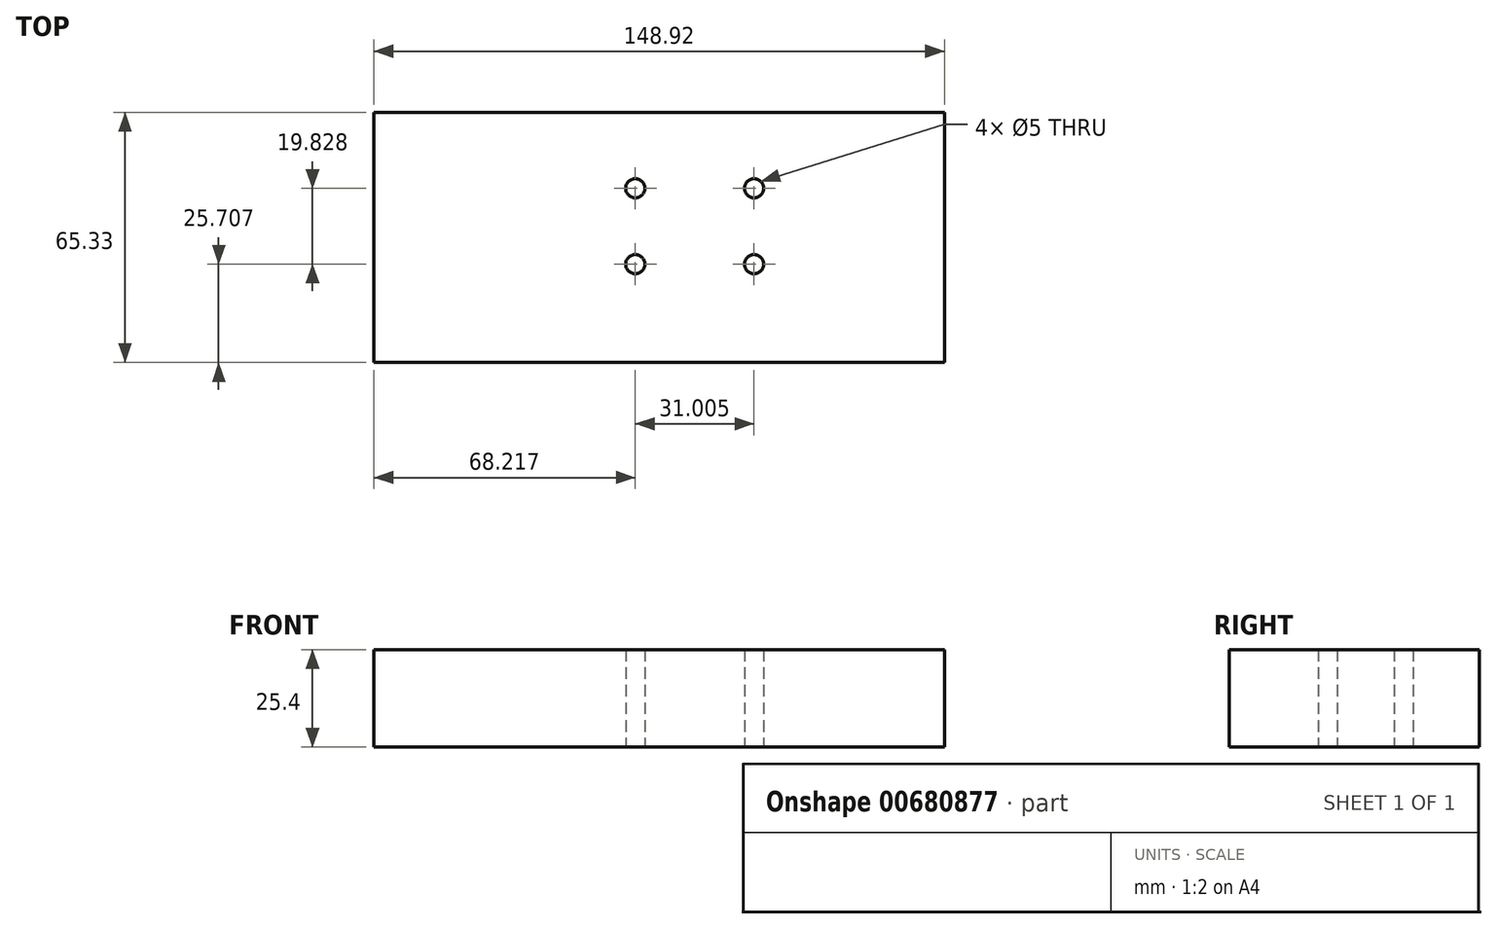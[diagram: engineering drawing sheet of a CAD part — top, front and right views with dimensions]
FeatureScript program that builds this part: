
annotation { "Feature Type Name" : "Feature", "Feature Type Description" : "" }
export const myFeature = defineFeature(function(context is Context, id is Id, definition is map)
    precondition{}
    {
        {
            var Q0;
            Q0=qCreatedBy(makeId("Top.planeOp"),FACE);
            var sketch = newSketch(context, id + "F0", { "sketchPlane" : qUnion([Q0])});
            skLineSegment(sketch, "E0.bottom", {"start": v(-106.28, 12.9) * mm, "end": v(42.64, 12.9) * mm});
            skLineSegment(sketch, "E0.top", {"start": v(-106.28, -52.43) * mm, "end": v(42.64, -52.43) * mm});
            skLineSegment(sketch, "E0.left", {"start": v(-106.28, 12.9) * mm, "end": v(-106.28, -52.43) * mm});
            skLineSegment(sketch, "E0.right", {"start": v(42.64, 12.9) * mm, "end": v(42.64, -52.43) * mm});
            skPoint(sketch, "E1", {"position": v(-63.68, -30.46) * mm});
            skPoint(sketch, "E2", {"position": v(-21.6, -30.46) * mm});
            skPoint(sketch, "E3", {"position": v(-21.6, -9.02) * mm});
            skPoint(sketch, "E4", {"position": v(-63.68, -9.02) * mm});
            skSolve(sketch);
        }
        {
            var Q0;
            Q0 = qSketchRegion(id + "F0", true);
            extrude(context, id + "F1", {"entities" : qUnion([Q0]), "depth" : 25.4 * mm, "offsetDistance" : 25.4 * mm});
        }
        {
            var Q0;
            Q0=makeQuery(id+"F1.opExtrude","CAP_FACE",FACE,{"disambiguationData":[OSD([sQuery(id+"F0.wireOp",EDGE,"E0.bottom"),sQuery(id+"F0.wireOp",EDGE,"E0.top"),sQuery(id+"F0.wireOp",EDGE,"E0.left"),sQuery(id+"F0.wireOp",EDGE,"E0.right")])],"isStart":true});
            var sketch = newSketch(context, id + "F2", { "sketchPlane" : qUnion([Q0])});
            skPoint(sketch, "E5", {"position": v(-7.06, 26.72) * mm});
            skPoint(sketch, "E6", {"position": v(-7.06, 6.9) * mm});
            skPoint(sketch, "E7", {"position": v(-38.06, 6.9) * mm});
            skPoint(sketch, "E8", {"position": v(-38.06, 26.72) * mm});
            skSolve(sketch);
        }
        {
            var Q0;
            Q0=sQuery(id+"F2.wireOp",VERTEX,"E5");
            var Q1;
            Q1=sQuery(id+"F2.wireOp",VERTEX,"E6");
            var Q2;
            Q2=sQuery(id+"F2.wireOp",VERTEX,"E8");
            var Q3;
            Q3=sQuery(id+"F2.wireOp",VERTEX,"E7");
            var Q4;
            Q4=makeQuery(id+"F1.opExtrude","SWEPT_BODY",BODY,{"disambiguationData":[OSD([sQuery(id+"F0.wireOp",EDGE,"E0.bottom"),sQuery(id+"F0.wireOp",EDGE,"E0.top"),sQuery(id+"F0.wireOp",EDGE,"E0.left"),sQuery(id+"F0.wireOp",EDGE,"E0.right")])]});
            hole(context, id + "F3", {"style" : HoleStyle.SIMPLE, "endStyle" : HoleEndStyle.THROUGH, "standardTappedOrClearance" : lookupTablePath({ "standard" : "ISO", "size" : "5", "type" : "Drilled" }), "standardBlindInLast" : lookupTablePath({ "standard" : "ISO", "size" : "5", "type" : "Drilled" }), "holeDiameter" : 5 * mm, "majorDiameter" : 6.35 * mm, "isTappedThrough" : true, "tappedDepth" : 12.7 * mm, "tapClearance" : 3, "locations" : qUnion([Q0, Q1, Q2, Q3]), "scope" : qUnion([Q4])});
        }
    });
